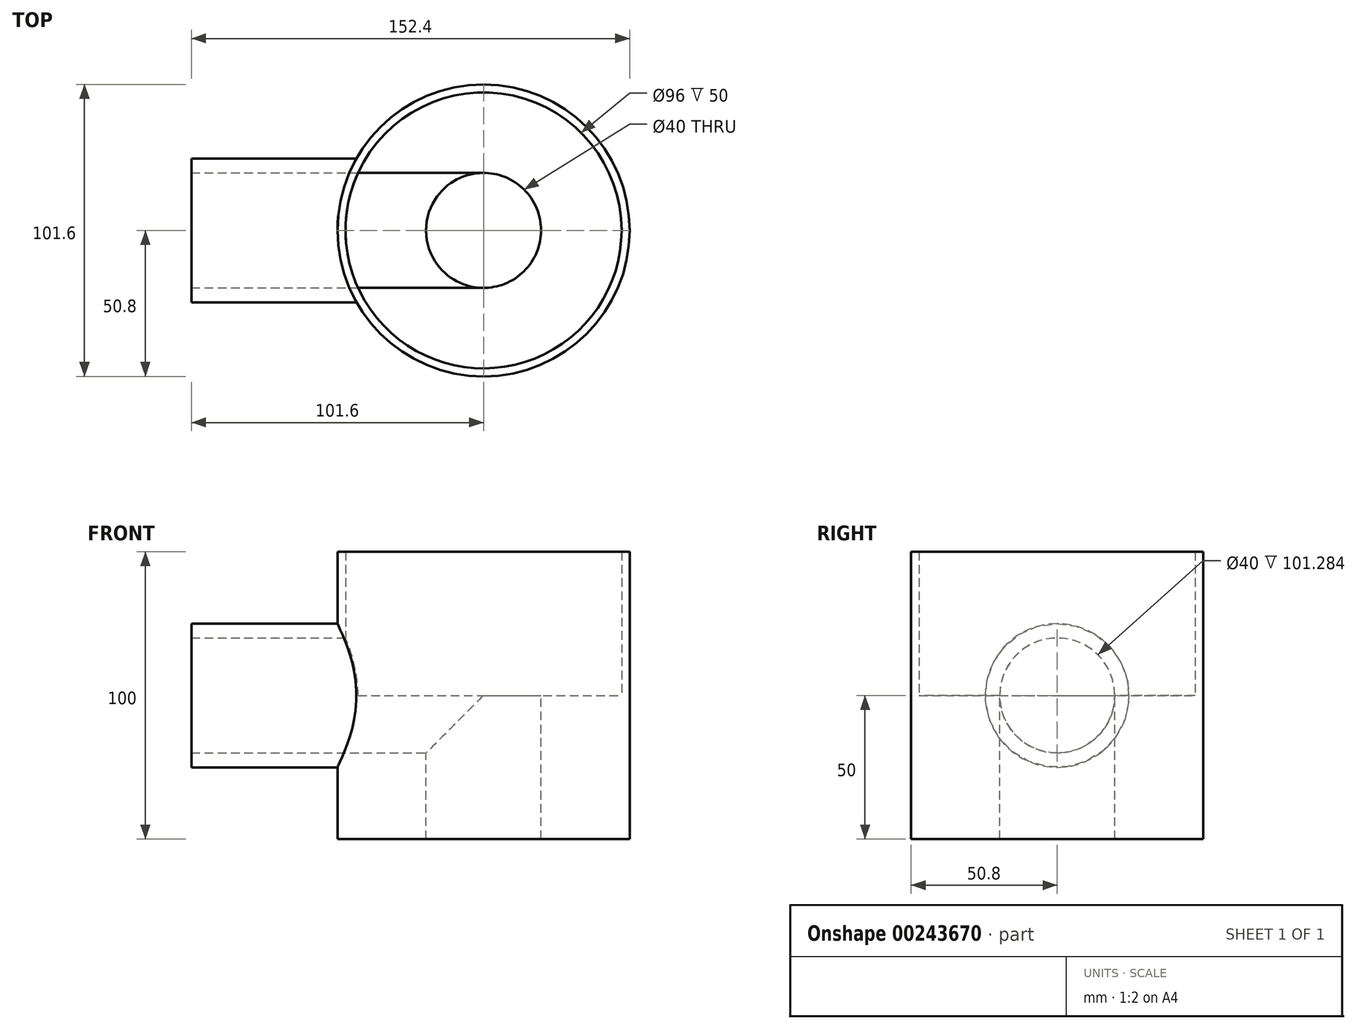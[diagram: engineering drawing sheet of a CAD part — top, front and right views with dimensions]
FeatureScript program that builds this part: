
annotation { "Feature Type Name" : "Feature", "Feature Type Description" : "" }
export const myFeature = defineFeature(function(context is Context, id is Id, definition is map)
    precondition{}
    {
        {
            var Q0;
            Q0=qCreatedBy(makeId("Top.planeOp"),FACE);
            var sketch = newSketch(context, id + "F0", { "sketchPlane" : qUnion([Q0])});
            skLineSegment(sketch, "E0.bottom", {"start": v(-50.8, -50.8) * mm, "end": v(50.8, -50.8) * mm, "construction": true});
            skLineSegment(sketch, "E0.top", {"start": v(-50.8, 50.8) * mm, "end": v(50.8, 50.8) * mm, "construction": true});
            skLineSegment(sketch, "E0.left", {"start": v(-50.8, -50.8) * mm, "end": v(-50.8, 50.8) * mm, "construction": true});
            skLineSegment(sketch, "E0.right", {"start": v(50.8, -50.8) * mm, "end": v(50.8, 50.8) * mm, "construction": true});
            skPoint(sketch, "E0.middle", {"position": v(0, 0) * mm});
            skCircle(sketch, "E1", {"center": v(0, 0) * mm, "radius": 48 * mm});
            skCircle(sketch, "E2", {"center": v(0, 0) * mm, "radius": 50.8 * mm});
            skSolve(sketch);
        }
        {
            var Q0;
            Q0=makeQuery(id+"F0.imprint","IMPRINT",FACE,{"disambiguationData":[TD([[makeQuery(id+"F0.imprint","IMPRINT",EDGE,{"derivedFrom":sQuery(id+"F0.wireOp",EDGE,"E1")}),-1.0]])]});
            extrude(context, id + "F1", {"entities" : qUnion([Q0]), "endBound" : BoundingType.SYMMETRIC, "depth" : 100 * mm});
        }
        {
            var Q0;
            Q0=qCreatedBy(makeId("Top.planeOp"),FACE);
            var sketch = newSketch(context, id + "F2", { "sketchPlane" : qUnion([Q0])});
            skCircle(sketch, "E3", {"center": v(0, 0) * mm, "radius": 50.8 * mm});
            skCircle(sketch, "E4", {"center": v(0, 0) * mm, "radius": 20 * mm});
            skSolve(sketch);
        }
        {
            var Q0;
            Q0=makeQuery(id+"F2.imprint","IMPRINT",FACE,{"disambiguationData":[TD([[makeQuery(id+"F2.imprint","IMPRINT",EDGE,{"derivedFrom":sQuery(id+"F2.wireOp",EDGE,"E3")}),1.0]])]});
            var Q1;
            Q1=makeQuery(id+"F1.opExtrude","CAP_FACE",FACE,{"disambiguationData":[OSD([sQuery(id+"F0.wireOp",EDGE,"E1"),sQuery(id+"F0.wireOp",EDGE,"E2")])],"isStart":true});
            extrude(context, id + "F3", {"entities" : qUnion([Q0]), "operationType" : NewBodyOperationType.ADD, "endBound" : BoundingType.UP_TO_SURFACE, "oppositeDirection" : true, "endBoundEntityFace" : qUnion([Q1]), "depth" : 25.4 * mm});
        }
        {
            var Q0;
            Q0=qCreatedBy(makeId("Right.planeOp"),FACE);
            var sketch = newSketch(context, id + "F4", { "sketchPlane" : qUnion([Q0])});
            skCircle(sketch, "E5", {"center": v(0, 0) * mm, "radius": 20 * mm});
            skSolve(sketch);
        }
        {
            var Q0;
            Q0=qSketchRegion(id+"F4",true);
            extrude(context, id + "F5", {"entities" : qUnion([Q0]), "operationType" : NewBodyOperationType.REMOVE, "endBound" : BoundingType.THROUGH_ALL, "oppositeDirection" : true, "depth" : 50.8 * mm});
        }
        {
            var Q0;
            Q0=qCreatedBy(makeId("Right.planeOp"),FACE);
            cPlane(context, id + "F6", {"entities" : qUnion([Q0]), "cplaneType" : CPlaneType.OFFSET, "offset" : 101.6 * mm, "oppositeDirection" : true, "width" : 152.4 * mm, "height" : 152.4 * mm});
        }
        {
            var Q0;
            Q0=qCreatedBy(id+"F6.planeOp",FACE);
            var sketch = newSketch(context, id + "F7", { "sketchPlane" : qUnion([Q0])});
            skCircle(sketch, "E6", {"center": v(0, 0) * mm, "radius": 25 * mm});
            skCircle(sketch, "E7", {"center": v(0, 0) * mm, "radius": 20 * mm});
            skSolve(sketch);
        }
        {
            var Q0;
            Q0 = qSketchRegion(id + "F7", true);
            extrude(context, id + "F8", {"entities" : qUnion([Q0]), "operationType" : NewBodyOperationType.ADD, "endBound" : BoundingType.UP_TO_NEXT, "depth" : 25.4 * mm});
        }
    });
